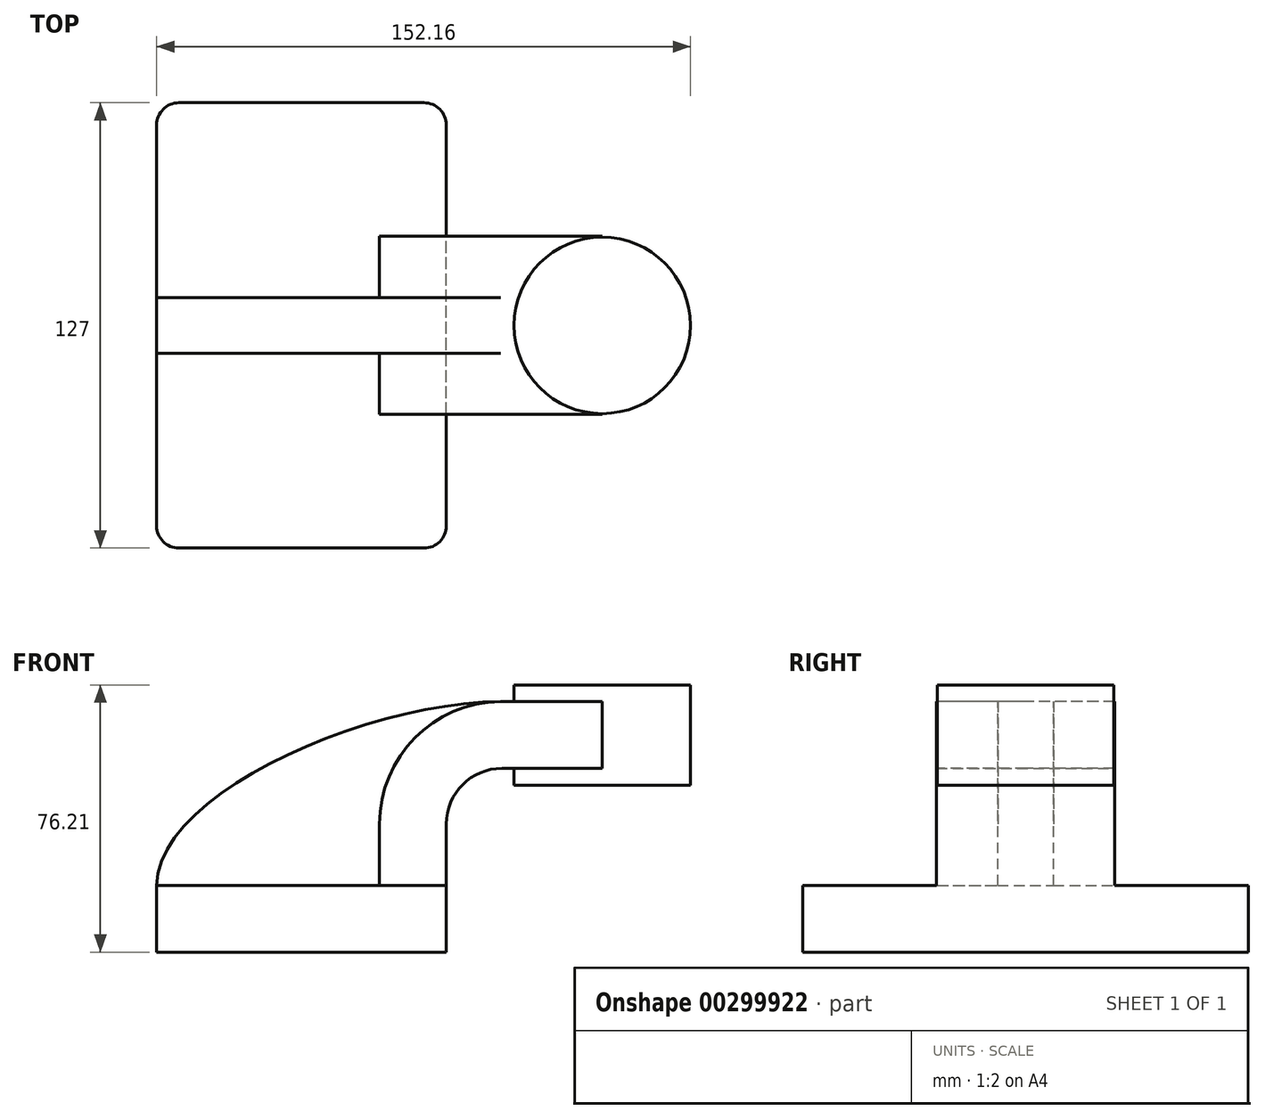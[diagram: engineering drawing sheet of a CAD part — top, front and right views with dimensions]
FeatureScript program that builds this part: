
annotation { "Feature Type Name" : "Feature", "Feature Type Description" : "" }
export const myFeature = defineFeature(function(context is Context, id is Id, definition is map)
    precondition{}
    {
        {
            var Q0;
            Q0=qCreatedBy(makeId("Front.planeOp"),FACE);
            var sketch = newSketch(context, id + "F0", { "sketchPlane" : qUnion([Q0])});
            skLineSegment(sketch, "E0.bottom", {"start": v(41.27, 9.53) * mm, "end": v(-41.28, 9.53) * mm});
            skLineSegment(sketch, "E0.top", {"start": v(41.28, -9.52) * mm, "end": v(-41.27, -9.52) * mm});
            skLineSegment(sketch, "E0.left", {"start": v(41.27, 9.53) * mm, "end": v(41.28, -9.52) * mm});
            skLineSegment(sketch, "E0.right", {"start": v(-41.28, 9.53) * mm, "end": v(-41.27, -9.52) * mm});
            skPoint(sketch, "E0.middle", {"position": v(0, 0) * mm});
            skLineSegment(sketch, "E1.bottom", {"start": v(60.08, 38.1) * mm, "end": v(110.88, 38.1) * mm});
            skLineSegment(sketch, "E1.top", {"start": v(60.08, 66.68) * mm, "end": v(110.88, 66.68) * mm});
            skLineSegment(sketch, "E1.left", {"start": v(60.08, 38.1) * mm, "end": v(60.08, 66.68) * mm});
            skLineSegment(sketch, "E1.right", {"start": v(110.88, 38.1) * mm, "end": v(110.88, 66.68) * mm});
            skPoint(sketch, "E1.middle", {"position": v(85.48, 52.39) * mm});
            skLineSegment(sketch, "E2", {"start": v(41.27, 9.53) * mm, "end": v(41.27, 27) * mm});
            skArc(sketch, "E3", {"start": v(41.27, 27) * mm, "mid": v(45.92, 38.23) * mm, "end": v(57.15, 42.88) * mm});
            skLineSegment(sketch, "E4", {"start": v(57.15, 42.88) * mm, "end": v(85.72, 42.88) * mm});
            skLineSegment(sketch, "E5.0", {"start": v(57.15, 61.93) * mm, "end": v(85.72, 61.93) * mm});
            skArc(sketch, "E5.1", {"start": v(22.22, 27) * mm, "mid": v(32.45, 51.7) * mm, "end": v(57.15, 61.93) * mm});
            skLineSegment(sketch, "E5.2", {"start": v(22.22, 9.53) * mm, "end": v(22.22, 27) * mm});
            skLineSegment(sketch, "E6", {"start": v(85.72, 38.1) * mm, "end": v(85.72, 66.68) * mm});
            skFitSpline(sketch, "E7", {"points": [v(-41.28, 9.53) * mm, v(57.15, 61.93) * mm], "startDerivative": vector(1.01, 79.13) * mm, "endDerivative": vector(115.62, 0.36) * mm});
            skSolve(sketch);
        }
        {
            var Q0;
            Q0=makeQuery(id+"F0.imprint","IMPRINT",FACE,{"disambiguationData":[TD([[makeQuery(id+"F0.imprint","IMPRINT",EDGE,{"derivedFrom":sQuery(id+"F0.wireOp",EDGE,"E0.top")}),-1.0]])]});
            extrude(context, id + "F1", {"entities" : qUnion([Q0]), "endBound" : BoundingType.SYMMETRIC, "depth" : 127 * mm});
        }
        {
            var Q0;
            {var subQ1=sQuery(id+"F0.wireOp",EDGE,"E2");Q0=makeQuery(id+"F0.imprint","IMPRINT",FACE,{"disambiguationData":[TD([[makeQuery(id+"F0.imprint","IMPRINT",EDGE,{"derivedFrom":subQ1}),1.0]])]});}
            var Q1;
            {var subQ0=sQuery(id+"F0.wireOp",EDGE,"E4");var subQ1=sQuery(id+"F0.wireOp",EDGE,"E1.left");var subQ2=makeQuery(id+"F0.imprint","INTERSECT",VERTEX,{"derivedFrom":[subQ1,subQ0]});Q1=makeQuery(id+"F0.imprint","IMPRINT",FACE,{"disambiguationData":[TD([[makeQuery(id+"F0.imprint","IMPRINT",EDGE,{"disambiguationData":[TD([[subQ2,-1.0]])],"derivedFrom":subQ1}),-1.0]])]});}
            extrude(context, id + "F2", {"entities" : qUnion([Q0, Q1]), "operationType" : NewBodyOperationType.ADD, "endBound" : BoundingType.SYMMETRIC, "depth" : 50.8 * mm});
        }
        {
            var Q0;
            {var subQ3=sQuery(id+"F0.wireOp",EDGE,"E5.2");Q0=makeQuery(id+"F0.imprint","IMPRINT",FACE,{"disambiguationData":[TD([[makeQuery(id+"F0.imprint","IMPRINT",EDGE,{"derivedFrom":subQ3}),1.0]])]});}
            extrude(context, id + "F3", {"entities" : qUnion([Q0]), "operationType" : NewBodyOperationType.ADD, "endBound" : BoundingType.SYMMETRIC, "depth" : 15.88 * mm});
        }
        {
            var Q0;
            {var subQ4=sQuery(id+"F0.wireOp",EDGE,"E1.right");Q0=makeQuery(id+"F0.imprint","IMPRINT",FACE,{"disambiguationData":[TD([[makeQuery(id+"F0.imprint","IMPRINT",EDGE,{"derivedFrom":subQ4}),1.0]])]});}
            var Q1;
            Q1=sQuery(id+"F0.wireOp",EDGE,"E6");
            revolve(context, id + "F4", {"operationType" : NewBodyOperationType.ADD, "entities" : qUnion([Q0]), "axis" : qUnion([Q1]), "revolveType" : RevolveType.FULL});
        }
        {
            var Q0;
            Q0=makeQuery(id+"F1.opExtrude","CAP_EDGE",EDGE,{"disambiguationData":[OSD([sQuery(id+"F0.wireOp",EDGE,"E0.right")])],"isStart":true});
            var Q1;
            Q1=makeQuery(id+"F1.opExtrude","CAP_EDGE",EDGE,{"disambiguationData":[OSD([sQuery(id+"F0.wireOp",EDGE,"E0.right")])],"isStart":false});
            var Q2;
            Q2=makeQuery(id+"F1.opExtrude","CAP_EDGE",EDGE,{"disambiguationData":[OSD([sQuery(id+"F0.wireOp",EDGE,"E0.left")])],"isStart":false});
            var Q3;
            Q3=makeQuery(id+"F1.opExtrude","CAP_EDGE",EDGE,{"disambiguationData":[OSD([sQuery(id+"F0.wireOp",EDGE,"E0.left")])],"isStart":true});
            fillet(context, id + "F5", {"entities" : qUnion([Q0, Q1, Q2, Q3]), "radius" : 6.35 * mm, "tangentPropagation" : true, "allowEdgeOverflow" : false});
        }
    });
